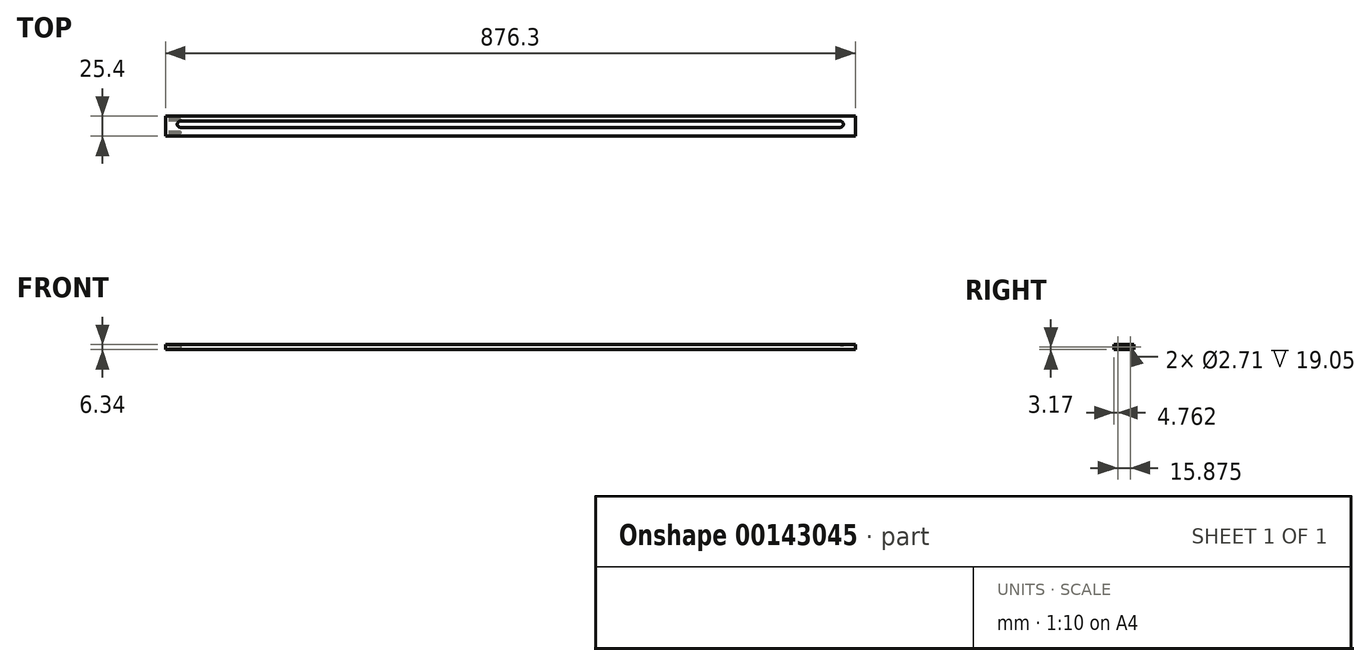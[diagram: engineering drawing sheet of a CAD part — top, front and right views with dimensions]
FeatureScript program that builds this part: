
annotation { "Feature Type Name" : "Feature", "Feature Type Description" : "" }
export const myFeature = defineFeature(function(context is Context, id is Id, definition is map)
    precondition{}
    {
        {
            var Q0;
            Q0=qCreatedBy(makeId("Top.planeOp"),FACE);
            var sketch = newSketch(context, id + "F0", { "sketchPlane" : qUnion([Q0])});
            skLineSegment(sketch, "E0.bottom", {"start": v(-438.15, 12.7) * mm, "end": v(438.15, 12.7) * mm});
            skLineSegment(sketch, "E0.top", {"start": v(-438.15, -12.7) * mm, "end": v(438.15, -12.7) * mm});
            skLineSegment(sketch, "E0.left", {"start": v(-438.15, 12.7) * mm, "end": v(-438.15, -12.7) * mm});
            skLineSegment(sketch, "E0.right", {"start": v(438.15, 12.7) * mm, "end": v(438.15, -12.7) * mm});
            skPoint(sketch, "E0.middle", {"position": v(0, 0) * mm});
            skSolve(sketch);
        }
        {
            var Q0;
            Q0 = qSketchRegion(id + "F0", true);
            extrude(context, id + "F1", {"entities" : qUnion([Q0]), "endBound" : BoundingType.SYMMETRIC, "depth" : 6.35 * mm});
        }
        {
            var Q0;
            Q0=makeQuery(id+"F1.opExtrude","SWEPT_FACE",FACE,{"disambiguationData":[OSD([sQuery(id+"F0.wireOp",EDGE,"E0.left")])]});
            var sketch = newSketch(context, id + "F2", { "sketchPlane" : qUnion([Q0])});
            skLineSegment(sketch, "E1", {"start": v(-7.94, 0) * mm, "end": v(7.94, 0) * mm, "construction": true});
            skCircle(sketch, "E2", {"center": v(-7.94, 0) * mm, "radius": 1.35 * mm});
            skCircle(sketch, "E3", {"center": v(7.94, 0) * mm, "radius": 1.35 * mm});
            skSolve(sketch);
        }
        {
            var Q0;
            Q0 = qSketchRegion(id + "F2", true);
            extrude(context, id + "F3", {"entities" : qUnion([Q0]), "operationType" : NewBodyOperationType.REMOVE, "oppositeDirection" : true, "depth" : 19.05 * mm});
        }
        {
            var Q0;
            Q0=makeQuery(id+"F1.opExtrude","CAP_FACE",FACE,{"disambiguationData":[OSD([sQuery(id+"F0.wireOp",EDGE,"E0.bottom"),sQuery(id+"F0.wireOp",EDGE,"E0.top"),sQuery(id+"F0.wireOp",EDGE,"E0.left"),sQuery(id+"F0.wireOp",EDGE,"E0.right")])],"isStart":false});
            var sketch = newSketch(context, id + "F4", { "sketchPlane" : qUnion([Q0])});
            skLineSegment(sketch, "E4", {"start": v(419.1, 2.38) * mm, "end": v(-419.1, 2.38) * mm, "construction": true});
            skArc(sketch, "E5", {"start": v(419.1, -1.59) * mm, "mid": v(423.07, 2.38) * mm, "end": v(419.1, 6.35) * mm});
            skArc(sketch, "E6", {"start": v(-419.1, -1.59) * mm, "mid": v(-423.07, 2.38) * mm, "end": v(-419.1, 6.35) * mm});
            skLineSegment(sketch, "E7", {"start": v(419.1, 6.35) * mm, "end": v(-419.1, 6.35) * mm});
            skLineSegment(sketch, "E8", {"start": v(-419.1, -1.59) * mm, "end": v(419.1, -1.59) * mm});
            skLineSegment(sketch, "E9", {"start": v(0, 2.38) * mm, "end": v(0, 0) * mm, "construction": true});
            skSolve(sketch);
        }
        {
            var Q0;
            Q0 = qSketchRegion(id + "F4", true);
            extrude(context, id + "F5", {"entities" : qUnion([Q0]), "operationType" : NewBodyOperationType.REMOVE, "oppositeDirection" : true, "depth" : 0.8 * mm});
        }
    });
